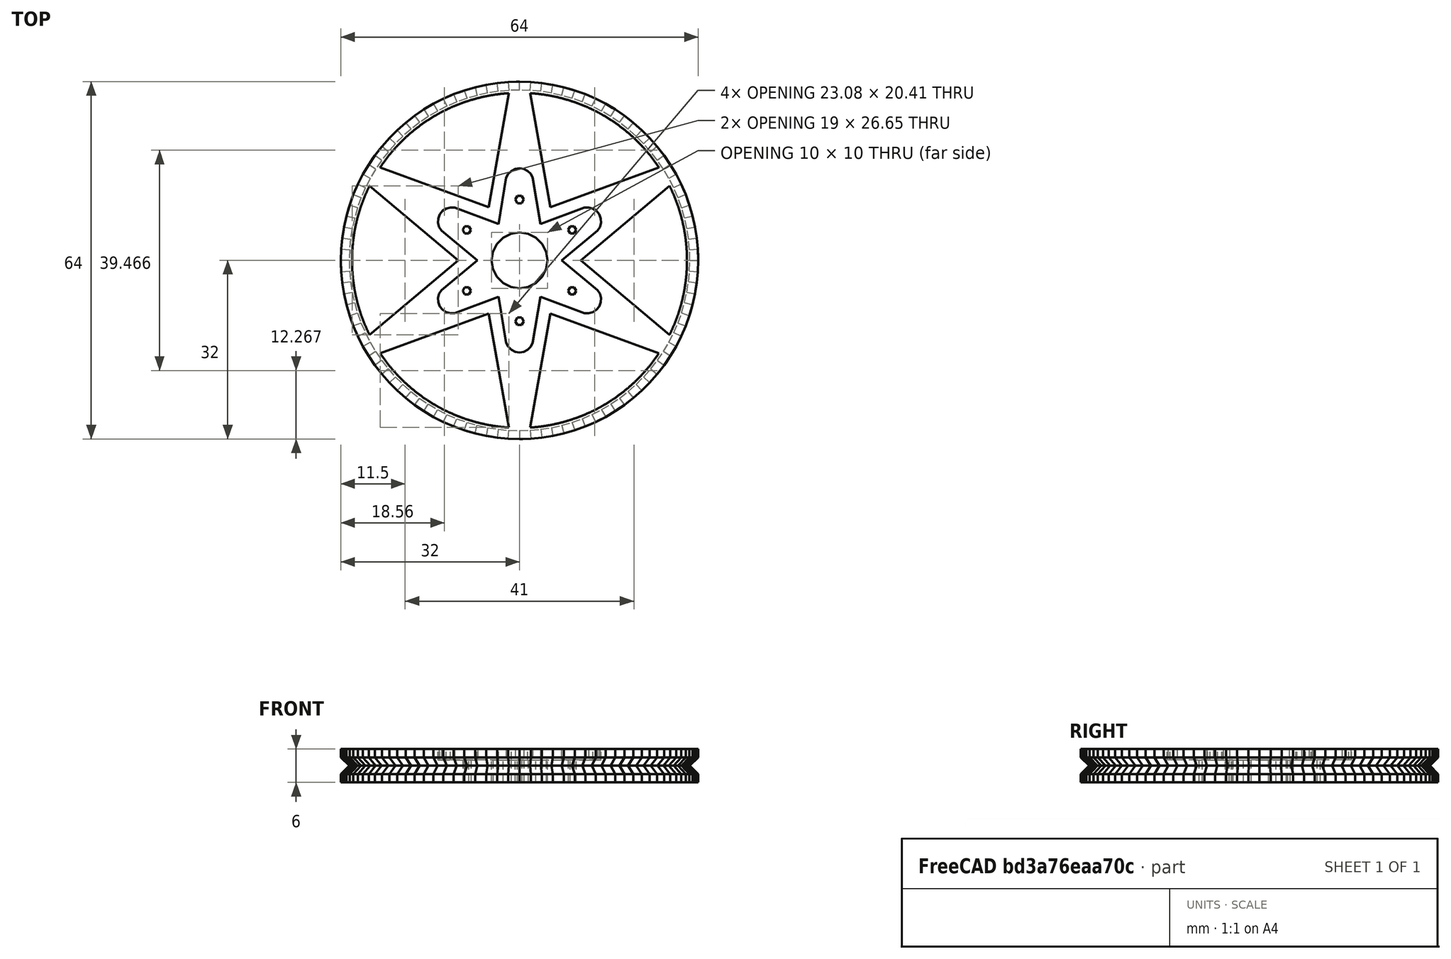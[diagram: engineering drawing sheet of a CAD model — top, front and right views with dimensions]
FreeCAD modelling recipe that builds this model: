
FCSTD DOCUMENT  (FreeCAD 0.16R6698 (Git))
Label: RuedaConRadios
License: All rights reserved
LicenseURL: http://es.wikipedia.org/wiki/Todos_los_derechos_reservados
objects: Part::Cylinder×2, Part::FeaturePython×1, Part::MultiCommon×1, Spreadsheet::Sheet×1, Part::Feature×1, Part::Cut×1
note: 6 computed .brp shape members not serialized (recipe doc carries the construction recipe); baked Part::Feature solids carry a one-line shape summary decoded from their .brp

FEATURE [Part::Cylinder] Cylinder  label="Cilindro"
  Angle = 80
  Height = 21
  Placement = pos=(11,0,-15) rot=(0,0,-1;0.698132rad)
  Radius = 21
  expr: Placement.Rotation.Angle = Spreadsheet.angulo / 2
FEATURE [Part::FeaturePython] Array  # Draft array (typed FeaturePython)
  Angle = 360
  ArrayType = 1
  Axis = (0,0,1)
  Base = -> Cylinder
  Center = (0,0,0)
  Fuse = false
  IntervalAxis = (0,0,0)
  IntervalX = (1,0,0)
  IntervalY = (0,1,0)
  IntervalZ = (0,0,0)
  NumberPolar = 6
  NumberX = 2
  NumberY = 2
  NumberZ = 1
FEATURE [Part::Cylinder] Cylinder001  label="Cilindro001"
  Angle = 360
  Height = 20
  Placement = pos=(0,0,-6) rot=(0,0,1;0rad)
  Radius = 30
FEATURE [Part::MultiCommon] Common
  Placement = pos=(0,0,-2) rot=(0,0,1;0rad)
  Shapes = -> [Cylinder001,Array]
FEATURE [Spreadsheet::Sheet] Spreadsheet
  cells = A1=Angulo Sector; B1(angulo)=80; A2=Radio; B2(radio)=22
FEATURE [Part::Feature] Servo_wheel_6_arms_58mm001_solid  label="Servo_wheel_6_arms_58mm001 (Solid)"
  shape: bbox 64 x 64 x 6 mm, 1920 faces (baked)
FEATURE [Part::Cut] Cut  label="RuedaHexRadial"
  Base = -> Servo_wheel_6_arms_58mm001_solid
  Tool = -> Common
